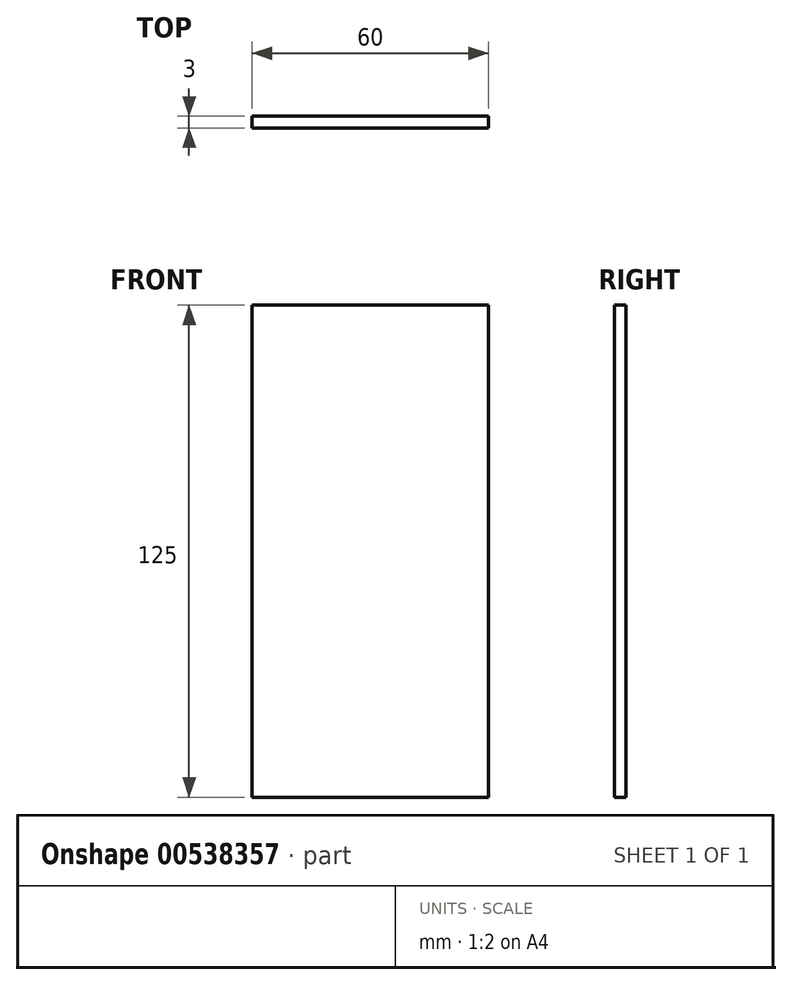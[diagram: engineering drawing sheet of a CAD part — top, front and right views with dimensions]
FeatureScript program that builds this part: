
annotation { "Feature Type Name" : "Feature", "Feature Type Description" : "" }
export const myFeature = defineFeature(function(context is Context, id is Id, definition is map)
    precondition{}
    {
        {
            var Q0;
            Q0=qCreatedBy(makeId("Right.planeOp"),FACE);
            var sketch = newSketch(context, id + "F0", { "sketchPlane" : qUnion([Q0])});
            skLineSegment(sketch, "E0.bottom", {"start": v(0, 0) * mm, "end": v(3, 0) * mm});
            skLineSegment(sketch, "E0.top", {"start": v(0, 125) * mm, "end": v(3, 125) * mm});
            skLineSegment(sketch, "E0.left", {"start": v(0, 0) * mm, "end": v(0, 125) * mm});
            skLineSegment(sketch, "E0.right", {"start": v(3, 0) * mm, "end": v(3, 125) * mm});
            skSolve(sketch);
        }
        {
            var Q0;
            Q0=makeQuery(id+"F0.imprint","IMPRINT",FACE,{"disambiguationData":[TD([[makeQuery(id+"F0.imprint","IMPRINT",EDGE,{"derivedFrom":sQuery(id+"F0.wireOp",EDGE,"E0.bottom")}),1.0]])]});
            extrude(context, id + "F1", {"entities" : qUnion([Q0]), "depth" : 60 * mm, "offsetDistance" : 25 * mm});
        }
    });
